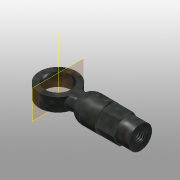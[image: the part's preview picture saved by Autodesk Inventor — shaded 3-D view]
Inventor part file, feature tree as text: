
AUTODESK INVENTOR PART (.ipt)
format: ipt  version: 2015 (Build 190159000, 159)  size: 188,928 bytes
history: native  units: mm
features: sketch x11, other x4, plane x1
ambient origin geometry x8: Origin, YZ Plane, XZ Plane, XY Plane, X Axis, Y Axis, Z Axis, Center Point
bodies: Solid1 (feature_tree)
feature tree (16):
  other  "500-000.ipt"
  other  "Solid1::500-000.ipt"
  other  "TaggingFeature1"
  sketch  "Sketch1"  dims[d0=10.0mm]
  sketch  "Sketch2"
  sketch  "Sketch3"
  sketch  "Sketch4"
  sketch  "Sketch5"
  sketch  "Sketch6"
  sketch  "Sketch9"
  sketch  "Sketch10"
  sketch  "Sketch11"
  sketch  "Sketch12"
  sketch  "Sketch13"
  plane  "Work Plane1"
  other  "Work Axis1"
